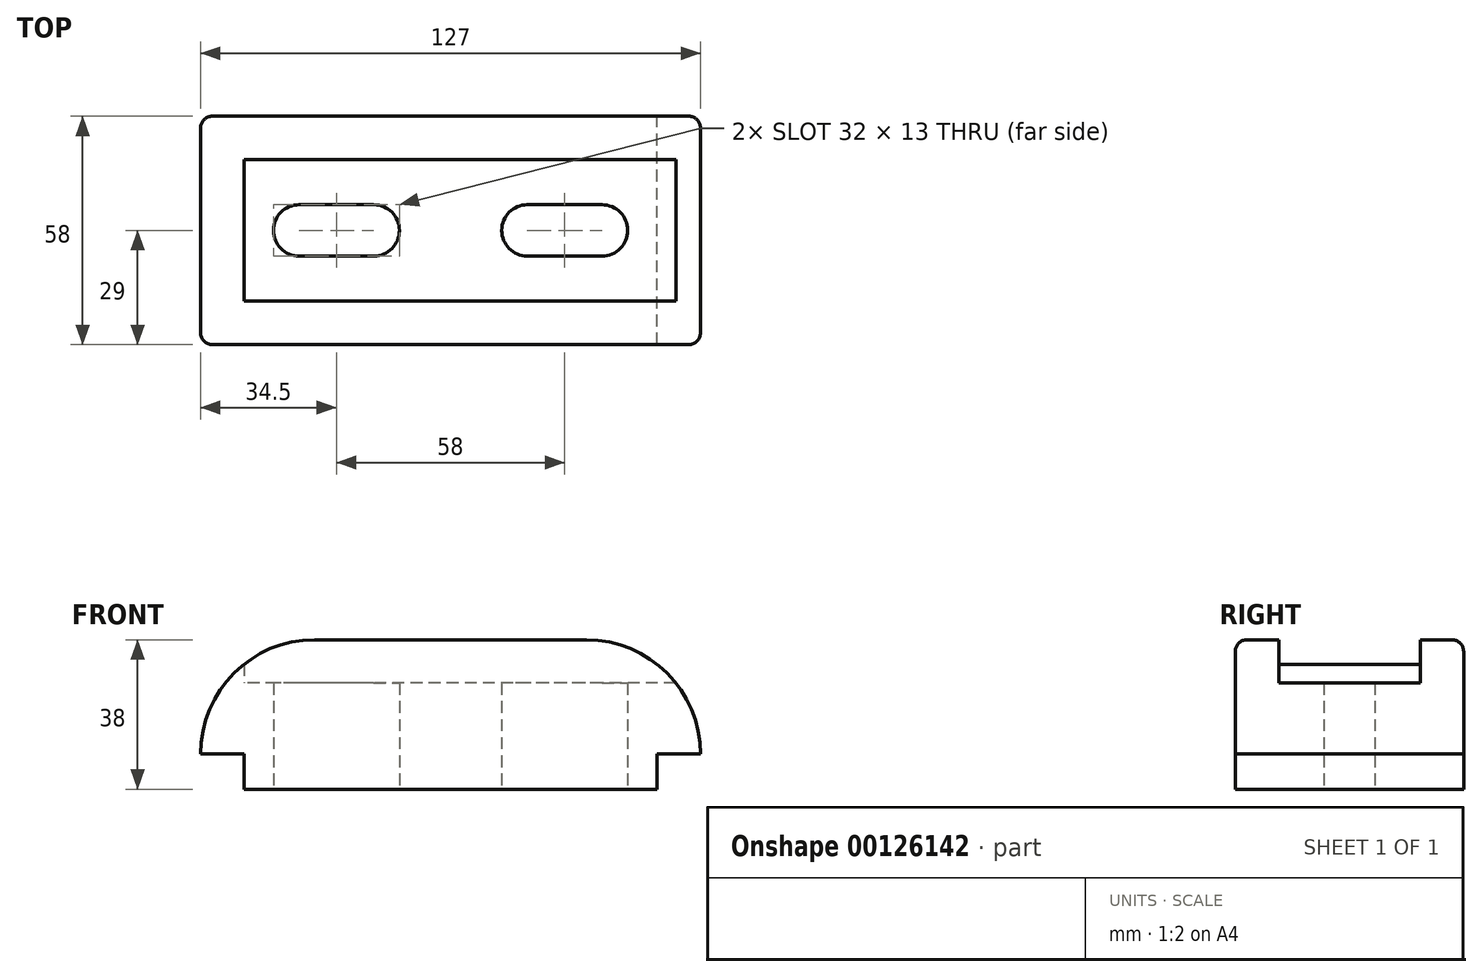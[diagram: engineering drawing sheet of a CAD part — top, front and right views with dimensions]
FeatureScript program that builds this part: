
annotation { "Feature Type Name" : "Feature", "Feature Type Description" : "" }
export const myFeature = defineFeature(function(context is Context, id is Id, definition is map)
    precondition{}
    {
        {
            var Q0;
            Q0=qCreatedBy(makeId("Front.planeOp"),FACE);
            var sketch = newSketch(context, id + "F0", { "sketchPlane" : qUnion([Q0])});
            skLineSegment(sketch, "E0", {"start": v(0, 0) * mm, "end": v(105, 0) * mm});
            skLineSegment(sketch, "E1", {"start": v(105, 0) * mm, "end": v(105, 9) * mm});
            skLineSegment(sketch, "E2", {"start": v(105, 9) * mm, "end": v(116, 9) * mm});
            skLineSegment(sketch, "E3", {"start": v(0, 0) * mm, "end": v(0, 9) * mm});
            skLineSegment(sketch, "E4", {"start": v(0, 9) * mm, "end": v(-11, 9) * mm});
            skLineSegment(sketch, "E5", {"start": v(18, 38) * mm, "end": v(87, 38) * mm});
            skArc(sketch, "E6", {"start": v(18, 38) * mm, "mid": v(-2.5, 29.5) * mm, "end": v(-11, 9) * mm});
            skArc(sketch, "E7", {"start": v(116, 9) * mm, "mid": v(107.5, 29.5) * mm, "end": v(87, 38) * mm});
            skSolve(sketch);
        }
        {
            var Q0;
            Q0 = qSketchRegion(id + "F0", true);
            extrude(context, id + "F1", {"entities" : qUnion([Q0]), "depth" : 58 * mm});
        }
        {
            var Q0;
            Q0=makeQuery(id+"F1.opExtrude","SWEPT_FACE",FACE,{"disambiguationData":[OSD([sQuery(id+"F0.wireOp",EDGE,"E0")])]});
            var sketch = newSketch(context, id + "F2", { "sketchPlane" : qUnion([Q0])});
            skLineSegment(sketch, "E8", {"start": v(0, 29) * mm, "end": v(105, 29) * mm, "construction": true});
            skLineSegment(sketch, "E9", {"start": v(14, 29) * mm, "end": v(14, 58) * mm, "construction": true});
            skLineSegment(sketch, "E10", {"start": v(33, 29) * mm, "end": v(33, 58) * mm, "construction": true});
            skLineSegment(sketch, "E11", {"start": v(91, 29) * mm, "end": v(91, 58) * mm, "construction": true});
            skLineSegment(sketch, "E12", {"start": v(72, 29) * mm, "end": v(72, 58) * mm, "construction": true});
            skLineSegment(sketch, "E13", {"start": v(14, 35.5) * mm, "end": v(33, 35.5) * mm});
            skLineSegment(sketch, "E14", {"start": v(72, 35.5) * mm, "end": v(91, 35.5) * mm});
            skLineSegment(sketch, "E15", {"start": v(91, 22.5) * mm, "end": v(72, 22.5) * mm});
            skLineSegment(sketch, "E16", {"start": v(14, 22.5) * mm, "end": v(33, 22.5) * mm});
            skArc(sketch, "E17", {"start": v(14, 35.5) * mm, "mid": v(7.5, 29) * mm, "end": v(14, 22.5) * mm});
            skArc(sketch, "E18", {"start": v(33, 22.5) * mm, "mid": v(39.5, 29) * mm, "end": v(33, 35.5) * mm});
            skArc(sketch, "E19", {"start": v(72, 35.5) * mm, "mid": v(65.5, 29) * mm, "end": v(72, 22.5) * mm});
            skArc(sketch, "E20", {"start": v(91, 22.5) * mm, "mid": v(97.5, 29) * mm, "end": v(91, 35.5) * mm});
            skSolve(sketch);
        }
        {
            var Q0;
            Q0 = qSketchRegion(id + "F2", true);
            extrude(context, id + "F3", {"entities" : qUnion([Q0]), "operationType" : NewBodyOperationType.REMOVE, "endBound" : BoundingType.THROUGH_ALL, "oppositeDirection" : true, "depth" : 25 * mm});
        }
        {
            var Q0;
            Q0=qCreatedBy(makeId("Right.planeOp"),FACE);
            var sketch = newSketch(context, id + "F4", { "sketchPlane" : qUnion([Q0])});
            skLineSegment(sketch, "E21.bottom", {"start": v(-11, 38) * mm, "end": v(-47, 38) * mm});
            skLineSegment(sketch, "E21.top", {"start": v(-11, 27) * mm, "end": v(-47, 27) * mm});
            skLineSegment(sketch, "E21.left", {"start": v(-11, 38) * mm, "end": v(-11, 27) * mm});
            skLineSegment(sketch, "E21.right", {"start": v(-47, 38) * mm, "end": v(-47, 27) * mm});
            skSolve(sketch);
        }
        {
            var Q0;
            Q0 = qSketchRegion(id + "F4", true);
            extrude(context, id + "F5", {"entities" : qUnion([Q0]), "operationType" : NewBodyOperationType.REMOVE, "endBound" : BoundingType.THROUGH_ALL, "depth" : 25 * mm});
        }
        {
            var Q0;
            Q0=makeQuery(id+"F1.opExtrude","CAP_EDGE",EDGE,{"disambiguationData":[OSD([sQuery(id+"F0.wireOp",EDGE,"E5")])],"isStart":false});
            var Q1;
            Q1=makeQuery(id+"F1.opExtrude","CAP_EDGE",EDGE,{"disambiguationData":[OSD([sQuery(id+"F0.wireOp",EDGE,"E5")])],"isStart":true});
            fillet(context, id + "F6", {"entities" : qUnion([Q0, Q1]), "radius" : 3 * mm, "tangentPropagation" : true, "allowEdgeOverflow" : false});
        }
    });
